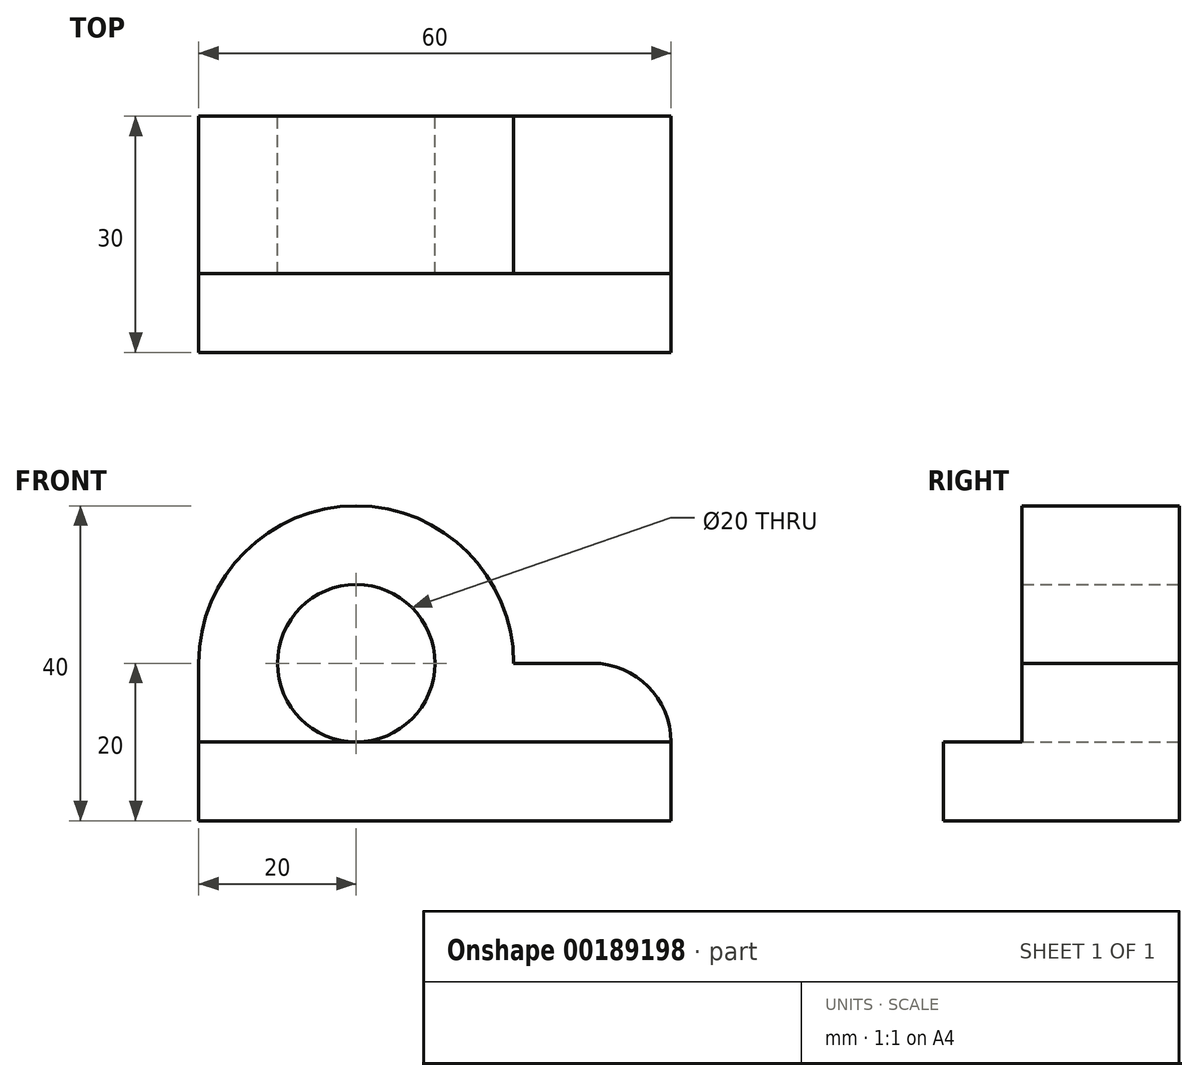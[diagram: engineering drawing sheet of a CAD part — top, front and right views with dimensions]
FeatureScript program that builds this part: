
annotation { "Feature Type Name" : "Feature", "Feature Type Description" : "" }
export const myFeature = defineFeature(function(context is Context, id is Id, definition is map)
    precondition{}
    {
        {
            var Q0;
            Q0=qCreatedBy(makeId("Front.planeOp"),FACE);
            var sketch = newSketch(context, id + "F0", { "sketchPlane" : qUnion([Q0])});
            skLineSegment(sketch, "E0", {"start": v(0, 0) * mm, "end": v(60, 0) * mm});
            skLineSegment(sketch, "E1", {"start": v(60, 0) * mm, "end": v(60, 10) * mm});
            skLineSegment(sketch, "E2", {"start": v(50, 20) * mm, "end": v(40, 20) * mm});
            skLineSegment(sketch, "E3", {"start": v(0, 0) * mm, "end": v(0, 20) * mm});
            skArc(sketch, "E4", {"start": v(40, 20) * mm, "mid": v(20, 40) * mm, "end": v(0, 20) * mm});
            skPoint(sketch, "E5.visualSharp", {"position": v(60, 20) * mm});
            skArc(sketch, "E5.filletArc", {"start": v(60, 10) * mm, "mid": v(57.07, 17.07) * mm, "end": v(50, 20) * mm});
            skCircle(sketch, "E6", {"center": v(20, 20) * mm, "radius": 10 * mm});
            skSolve(sketch);
        }
        {
            var Q0;
            Q0=makeQuery(id+"F0.imprint","IMPRINT",FACE,{"disambiguationData":[TD([[makeQuery(id+"F0.imprint","IMPRINT",EDGE,{"derivedFrom":sQuery(id+"F0.wireOp",EDGE,"E0")}),1.0]])]});
            extrude(context, id + "F1", {"entities" : qUnion([Q0]), "depth" : 20 * mm});
        }
        {
            var Q0;
            Q0=makeQuery(id+"F1.opExtrude","CAP_FACE",FACE,{"disambiguationData":[OSD([sQuery(id+"F0.wireOp",EDGE,"E0"),sQuery(id+"F0.wireOp",EDGE,"E1"),sQuery(id+"F0.wireOp",EDGE,"E2"),sQuery(id+"F0.wireOp",EDGE,"E3"),sQuery(id+"F0.wireOp",EDGE,"E4"),sQuery(id+"F0.wireOp",EDGE,"E5.filletArc"),sQuery(id+"F0.wireOp",EDGE,"E6")])],"isStart":false});
            var sketch = newSketch(context, id + "F2", { "sketchPlane" : qUnion([Q0])});
            skLineSegment(sketch, "E7.bottom", {"start": v(0, 0) * mm, "end": v(60, 0) * mm});
            skLineSegment(sketch, "E7.top", {"start": v(0, 10) * mm, "end": v(60, 10) * mm});
            skLineSegment(sketch, "E7.left", {"start": v(0, 0) * mm, "end": v(0, 10) * mm});
            skLineSegment(sketch, "E7.right", {"start": v(60, 0) * mm, "end": v(60, 10) * mm});
            skSolve(sketch);
        }
        {
            var Q0;
            Q0=makeQuery(id+"F2.imprint","IMPRINT",FACE,{"disambiguationData":[TD([[makeQuery(id+"F2.imprint","IMPRINT",EDGE,{"derivedFrom":sQuery(id+"F2.wireOp",EDGE,"E7.bottom")}),1.0]])]});
            extrude(context, id + "F3", {"entities" : qUnion([Q0]), "operationType" : NewBodyOperationType.ADD, "depth" : 10 * mm});
        }
    });
